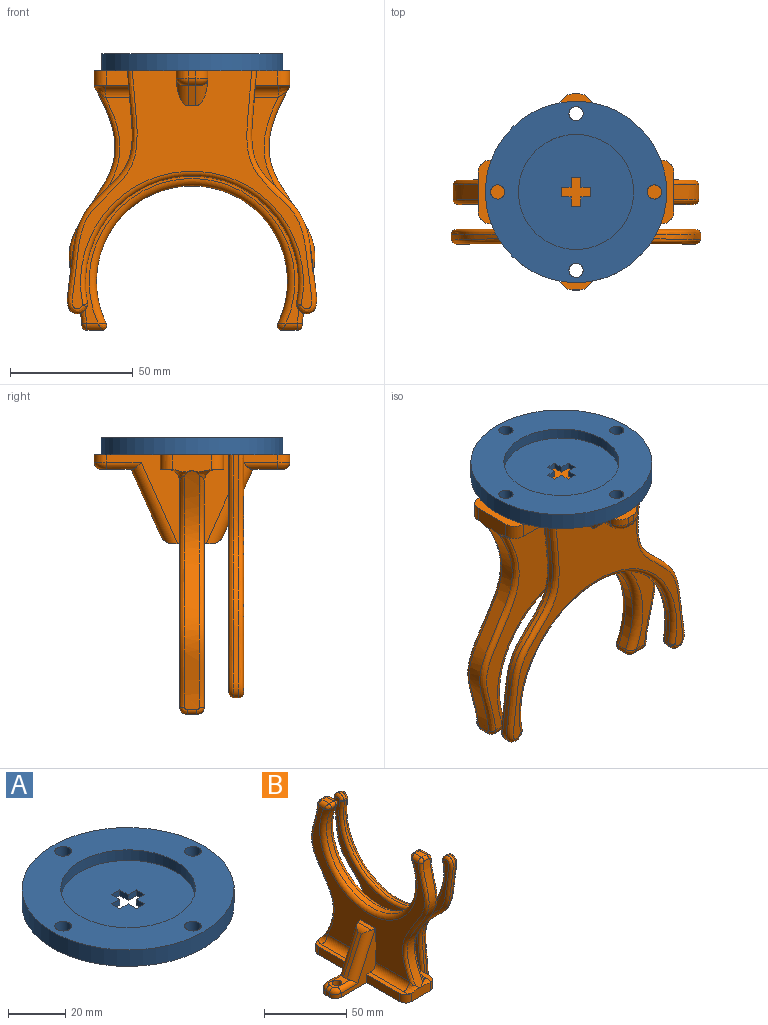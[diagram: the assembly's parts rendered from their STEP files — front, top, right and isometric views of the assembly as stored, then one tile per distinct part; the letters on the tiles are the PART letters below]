
ASSEMBLY  parts=2 mates=1
PART A: 21 faces, bbox 74x74x7 mm
  f0: cylinder r=37mm len=74mm, axis (0,0,1), area 1627.3mm2, adj f1,f2
  f1: plane 74x74mm, normal (0,0,1), area 2460.2mm2, adj f0,f3,f17,f18,f19,f20
  f2: plane 74x74mm, normal (0,0,-1), area 4115.2mm2, adj f0,f5,f6,f7,f8,f9,f10,f11
  f3: cylinder r=23.5mm len=47mm, axis (0,0,1), area 664.4mm2, adj f1,f4
  f4: plane 47x47mm, normal (0,0,1), area 1654.9mm2, adj f3,f5,f6,f7,f8,f9,f10,f11
  f5: plane 4x2.5mm, normal (1,0,0), area 10mm2, adj f2,f4,f7,f15
  f6: plane 4x2.5mm, normal (-1,0,0), area 10mm2, adj f2,f4,f9,f12
  f7: plane 4x2.5mm, normal (0,1,0), area 10mm2, adj f2,f4,f5,f10
  f8: plane 4x2.5mm, normal (1,0,0), area 10mm2, adj f2,f4,f9,f14
  f9: plane 4x2.5mm, normal (0,-1,0), area 10mm2, adj f2,f4,f6,f8
  f10: plane 4x2.5mm, normal (-1,0,0), area 10mm2, adj f2,f4,f7,f13
  f11: plane 4x2.5mm, normal (-1,0,0), area 10mm2, adj f2,f4,f12,f13
  f12: plane 4x2.5mm, normal (0,-1,0), area 10mm2, adj f2,f4,f6,f11
  f13: plane 4x2.5mm, normal (0,1,0), area 10mm2, adj f2,f4,f10,f11
  f14: plane 4x2.5mm, normal (0,-1,0), area 10mm2, adj f2,f4,f8,f16
  f15: plane 4x2.5mm, normal (0,1,0), area 10mm2, adj f2,f4,f5,f16
  f16: plane 4x2.5mm, normal (1,0,0), area 10mm2, adj f2,f4,f14,f15
  f17: cylinder r=2.9mm len=7mm, axis (0,0,1), area 127.5mm2, adj f1,f2
  f18: cylinder r=2.9mm len=7mm, axis (0,0,1), area 127.5mm2, adj f1,f2
  f19: cylinder r=2.9mm len=7mm, axis (0,0,1), area 127.5mm2, adj f1,f2
  f20: cylinder r=2.9mm len=7mm, axis (0,0,1), area 127.5mm2, adj f1,f2
PART B: 108 faces, bbox 80.1x101.9x109 mm
  f0: plane 36.25x10.1mm, normal (0,-1,0), area 217mm2, adj f3,f8,f15,f19,f33,f55,f57,f95
  f1: plane 36.25x10.1mm, normal (0,1,0), area 217mm2, adj f4,f7,f12,f15,f23,f33,f57,f95
  f2: plane 5.49x3mm, normal (0.91,0,0.41), area 18mm2, adj f3,f4,f63,f95
  f3: cylinder r=5mm len=22.73mm, axis (0.41,0,-0.91), area 102.8mm2, adj f0,f2,f57,f63,f95
  f4: cylinder r=5mm len=22.73mm, axis (-0.41,0,0.91), area 102.8mm2, adj f1,f2,f57,f63,f95
  f5: extruded ~97.66x18.78mm, area 618.1mm2, adj f43,f44,f45,f51,f53,f83,f90
  f6: extruded ~97.66x18.78mm, area 618.1mm2, adj f46,f47,f48,f54,f56,f77,f84
  f7: plane 33.48x4.5mm, normal (0,0,1), area 97.5mm2, adj f1,f12,f23,f39,f56
  f8: plane 33.48x4.5mm, normal (0,0,1), area 97.5mm2, adj f0,f19,f38,f53,f55
  f9: plane 33.48x4.5mm, normal (0,0,1), area 97.5mm2, adj f16,f17,f37,f51,f52
  f10: plane 12.7x7.09mm, normal (0,0,1), area 57.5mm2, adj f28,f60,f64,f65,f72,f73,f74,f75
  f11: cylinder r=5mm len=28.64mm, axis (0,-1,0), area 224.9mm2, adj f14,f26,f34,f54
  f12: cylinder r=5mm len=28.64mm, axis (0,1,0), area 224.9mm2, adj f1,f7,f33,f56
  f13: plane 12.7x7.09mm, normal (0,0,1), area 57.5mm2, adj f29,f58,f61,f62,f67,f68,f69,f70
  f14: plane 33.48x4.5mm, normal (0,0,1), area 97.5mm2, adj f11,f25,f26,f40,f54
  f15: plane 80.07x80.07mm, normal (0,0,-1), area 2921.5mm2, adj f0,f1,f16,f17,f18,f19,f20,f21
  f16: plane 36.25x30mm, normal (0,-1,0), area 312mm2, adj f9,f15,f17,f34,f36,f52,f59,f64
  f17: plane 28.5x6mm, normal (-1,0,0), area 171mm2, adj f9,f15,f16,f37
  f18: plane 16x6.99mm, normal (0,-1,0), area 105.5mm2, adj f15,f37,f38,f51,f53
  f19: plane 28.5x6mm, normal (1,0,0), area 171mm2, adj f0,f8,f15,f38
  f20: plane 13.9x3mm, normal (0,-1,0), area 41.7mm2, adj f15,f42,f67,f94
  f21: plane 3x3mm, normal (1,0,0), area 9mm2, adj f15,f41,f42,f69
  f22: plane 13.9x3mm, normal (0,1,0), area 41.7mm2, adj f15,f41,f71,f94
  f23: plane 28.5x6mm, normal (1,0,0), area 171mm2, adj f1,f7,f15,f39
  f24: plane 16x6.99mm, normal (0,1,0), area 105.5mm2, adj f15,f39,f40,f54,f56
  f25: plane 28.5x6mm, normal (-1,0,0), area 171mm2, adj f14,f15,f26,f40
  f26: plane 36.25x30mm, normal (0,1,0), area 312mm2, adj f11,f14,f15,f25,f34,f35,f59,f65
  f27: plane 3x3mm, normal (-1,0,0), area 9mm2, adj f15,f35,f36,f74
  f28: cylinder r=2.9mm len=6mm, axis (0,0,-1), area 109.3mm2, adj f10,f15
  f29: cylinder r=2.9mm len=6mm, axis (0,0,-1), area 109.3mm2, adj f13,f15
  f30: plane 6.06x4mm, normal (0,0,1), area 24.2mm2, adj f45,f50,f82,f89
  f31: plane 6.06x4mm, normal (0,0,1), area 24.2mm2, adj f48,f49,f78,f85
  f32: cylinder r=39mm len=78mm, axis (-1,0,0), area 631.9mm2, adj f49,f50,f80,f87
  f33: plane 96.41x92.04mm, normal (1,0,0), area 2688.9mm2, adj f0,f1,f12,f43,f46,f55,f57,f78
  f34: plane 96.41x92.04mm, normal (-1,0,0), area 2689.4mm2, adj f11,f16,f26,f44,f47,f52,f59,f85
  f35: cylinder r=5mm len=5mm, axis (0,0,1), area 23.6mm2, adj f15,f26,f27,f75
  f36: cylinder r=5mm len=5mm, axis (0,0,-1), area 23.6mm2, adj f15,f16,f27,f73
  f37: cylinder r=5mm len=6.02mm, axis (0,0,-1), area 47.1mm2, adj f9,f15,f17,f18,f51
  f38: cylinder r=5mm len=6.02mm, axis (0,0,1), area 47.1mm2, adj f8,f15,f18,f19,f53
  f39: cylinder r=5mm len=6.02mm, axis (0,0,-1), area 47.1mm2, adj f7,f15,f23,f24,f56
  f40: cylinder r=5mm len=6.02mm, axis (0,0,1), area 47.1mm2, adj f14,f15,f24,f25,f54
  f41: cylinder r=5mm len=5mm, axis (0,0,-1), area 23.6mm2, adj f15,f21,f22,f70
  f42: cylinder r=5mm len=5mm, axis (0,0,1), area 23.6mm2, adj f15,f20,f21,f68
  f43: bspline ~98.27x20.83mm, area 312.4mm2, adj f5,f33,f53,f83
  f44: bspline ~100.59x20.82mm, area 312.4mm2, adj f5,f34,f51,f90
  f45: cylinder r=2mm len=4mm, axis (-1,0,0), area 12.2mm2, adj f5,f30,f83,f90
  f46: bspline ~100.59x20.82mm, area 312.4mm2, adj f6,f33,f56,f77
  f47: bspline ~98.27x20.83mm, area 312.4mm2, adj f6,f34,f54,f84
  f48: cylinder r=2mm len=4mm, axis (-1,0,0), area 12.2mm2, adj f6,f31,f77,f84
  f49: cylinder r=2mm len=4mm, axis (-1,0,0), area 16.2mm2, adj f31,f32,f79,f86
  f50: cylinder r=2mm len=4mm, axis (-1,0,0), area 16.2mm2, adj f30,f32,f81,f88
  f51: bspline ~12.29x8.88mm, area 38mm2, adj f5,f9,f18,f37,f44,f52,f53
  f52: cylinder r=5mm len=28.64mm, axis (0,-1,0), area 224.9mm2, adj f9,f16,f34,f51
  f53: bspline ~12.29x8.88mm, area 38mm2, adj f5,f8,f18,f38,f43,f51,f55
  f54: bspline ~12.29x8.12mm, area 38mm2, adj f6,f11,f14,f24,f40,f47,f56
  f55: cylinder r=5mm len=28.64mm, axis (0,1,0), area 224.9mm2, adj f0,f8,f33,f53
  f56: bspline ~12.29x8.12mm, area 38mm2, adj f6,f7,f12,f24,f39,f46,f54
  f57: plane 13.02x3.1mm, normal (0,0,1), area 39.4mm2, adj f0,f1,f3,f4,f33,f63
  f58: plane 8.39x3.75mm, normal (0.91,0,0.41), area 27.6mm2, adj f13,f61,f62,f94
  f59: plane 13.02x3.1mm, normal (0,0,1), area 39.4mm2, adj f16,f26,f34,f64,f65,f66
  f60: plane 27.29x12.2mm, normal (-0.91,0,0.41), area 89.7mm2, adj f10,f64,f65,f66
  f61: cylinder r=5mm len=10.99mm, axis (0.41,0,-0.91), area 42.5mm2, adj f13,f58,f67,f94
  f62: cylinder r=5mm len=10.99mm, axis (-0.41,0,0.91), area 42.5mm2, adj f13,f58,f71,f94
  f63: cylinder r=5mm len=12.13mm, axis (0,1,0), area 43.5mm2, adj f2,f3,f4,f57
  f64: cylinder r=5mm len=35.29mm, axis (0.41,0,0.91), area 260.8mm2, adj f10,f16,f59,f60,f66,f72
  f65: cylinder r=5mm len=35.29mm, axis (-0.41,0,-0.91), area 260.8mm2, adj f10,f26,f59,f60,f66,f76
  f66: cylinder r=5mm len=12.13mm, axis (0,-1,0), area 43.5mm2, adj f59,f60,f64,f65
  f67: cylinder r=3mm len=13.9mm, axis (-1,0,0), area 57.6mm2, adj f13,f20,f61,f68,f94
  f68: torus R=2mm, axis (0,0,1), area 28.9mm2, adj f13,f42,f67,f69
  f69: cylinder r=3mm len=3mm, axis (0,-1,0), area 14.1mm2, adj f13,f21,f68,f70
  f70: torus R=2mm, axis (0,0,1), area 28.9mm2, adj f13,f41,f69,f71
  f71: cylinder r=3mm len=13.9mm, axis (1,0,0), area 57.6mm2, adj f13,f22,f62,f70,f94
  f72: cylinder r=3mm len=14.29mm, axis (-1,0,0), area 58.6mm2, adj f10,f16,f64,f73
  f73: torus R=2mm, axis (0,0,1), area 28.9mm2, adj f10,f36,f72,f74
  f74: cylinder r=3mm len=3mm, axis (0,1,0), area 14.1mm2, adj f10,f27,f73,f75
  f75: torus R=2mm, axis (0,0,1), area 28.9mm2, adj f10,f35,f74,f76
  f76: cylinder r=3mm len=14.29mm, axis (1,0,0), area 58.6mm2, adj f10,f26,f65,f75
  f77: bspline ~3.68x3.65mm, area 10.9mm2, adj f6,f46,f48,f78
  f78: cylinder r=3mm len=6.12mm, axis (0,1,0), area 25mm2, adj f31,f33,f77,f79
  f79: bspline ~3.56x3mm, area 9.8mm2, adj f49,f78,f80
  f80: torus R=42mm, axis (1,0,0), area 758mm2, adj f32,f33,f79,f81
  f81: bspline ~3.56x3mm, area 9.8mm2, adj f50,f80,f82
  f82: cylinder r=3mm len=6.12mm, axis (0,1,0), area 25mm2, adj f30,f33,f81,f83
  f83: bspline ~3.52x3.43mm, area 10.9mm2, adj f5,f43,f45,f82
  f84: bspline ~3.67x3.64mm, area 10.9mm2, adj f6,f47,f48,f85
  f85: cylinder r=3mm len=6.12mm, axis (0,-1,0), area 25mm2, adj f31,f34,f84,f86
  f86: bspline ~3.56x3mm, area 9.8mm2, adj f49,f85,f87
  f87: torus R=42mm, axis (1,0,0), area 758mm2, adj f32,f34,f86,f88
  f88: bspline ~3.56x3mm, area 9.8mm2, adj f50,f87,f89
  f89: cylinder r=3mm len=6.12mm, axis (0,-1,0), area 25mm2, adj f30,f34,f88,f90
  f90: bspline ~3.51x3.43mm, area 10.9mm2, adj f5,f44,f45,f89
  f91: extruded ~99.23x26.54mm, area 228.9mm2, adj f15,f102,f103,f107
  f92: cylinder r=43.5mm len=87mm, axis (1,0,0), area 308mm2, adj f98,f101,f104,f107
  f93: extruded ~99.23x26.54mm, area 228.9mm2, adj f15,f96,f97,f98
  f94: plane 97.84x97.27mm, normal (1,0,0), area 2328mm2, adj f15,f20,f22,f58,f61,f62,f67,f71
  f95: plane 97.84x97.27mm, normal (-1,0,0), area 2153.6mm2, adj f0,f1,f2,f3,f4,f15,f96,f101
  f96: bspline ~101.2x28.56mm, area 353.5mm2, adj f15,f93,f95,f99
  f97: bspline ~101.2x28.56mm, area 353.5mm2, adj f15,f93,f94,f100
  f98: cylinder r=2mm len=2mm, axis (1,0,0), area 2.9mm2, adj f92,f93,f99,f100
  f99: sphere r=2mm, area 2.2mm2, adj f96,f98,f101
  f100: sphere r=2mm, area 2.2mm2, adj f97,f98,f104
  f101: torus R=45.5mm, axis (1,0,0), area 491.8mm2, adj f92,f95,f99,f105
  f102: bspline ~101.2x28.56mm, area 353.5mm2, adj f15,f91,f95,f105
  f103: bspline ~101.2x28.56mm, area 353.5mm2, adj f15,f91,f94,f106
  f104: torus R=45.5mm, axis (1,0,0), area 491.8mm2, adj f92,f94,f100,f106
  f105: sphere r=2mm, area 2.2mm2, adj f101,f102,f107
  f106: sphere r=2mm, area 2.9mm2, adj f103,f104,f107
  f107: cylinder r=2mm len=2mm, axis (1,0,0), area 2.9mm2, adj f91,f92,f105,f106
PLACE A t=(0.72,0.32,3.35)mm
PLACE B rot(axis=(0.71,-0.71,0),180deg) t=(0.72,0.32,-3.65)mm
MATE fastened B.f28 <-> A.f19  axis (0,0,1) through (0.72,32.32,-3.65)mm
